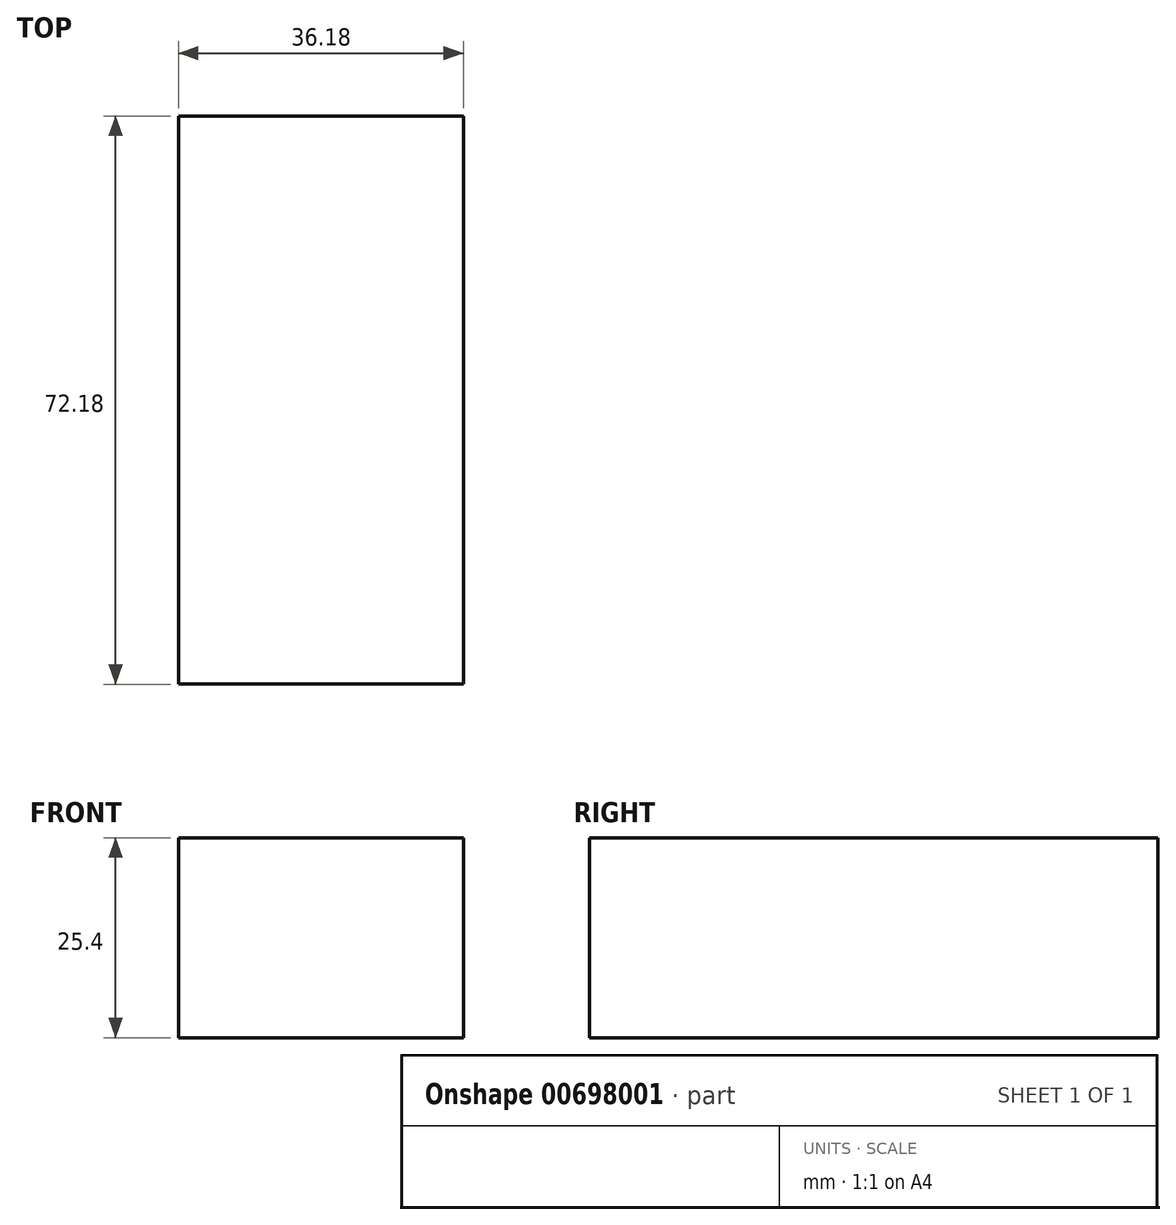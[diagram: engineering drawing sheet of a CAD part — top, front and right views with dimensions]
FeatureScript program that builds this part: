
annotation { "Feature Type Name" : "Feature", "Feature Type Description" : "" }
export const myFeature = defineFeature(function(context is Context, id is Id, definition is map)
    precondition{}
    {
        {
            var Q0;
            Q0=qCreatedBy(makeId("Top.planeOp"),FACE);
            var sketch = newSketch(context, id + "F0", { "sketchPlane" : qUnion([Q0])});
            skLineSegment(sketch, "E0.bottom", {"start": v(-14.17, -30.75) * mm, "end": v(22.01, -30.75) * mm});
            skLineSegment(sketch, "E0.top", {"start": v(-14.17, 41.43) * mm, "end": v(22.01, 41.43) * mm});
            skLineSegment(sketch, "E0.left", {"start": v(-14.17, -30.75) * mm, "end": v(-14.17, 41.43) * mm});
            skLineSegment(sketch, "E0.right", {"start": v(22.01, -30.75) * mm, "end": v(22.01, 41.43) * mm});
            skSolve(sketch);
        }
        {
            var Q0;
            Q0 = qSketchRegion(id + "F0", true);
            extrude(context, id + "F1", {"entities" : qUnion([Q0]), "depth" : 25.4 * mm, "offsetDistance" : 25.4 * mm});
        }
    });
